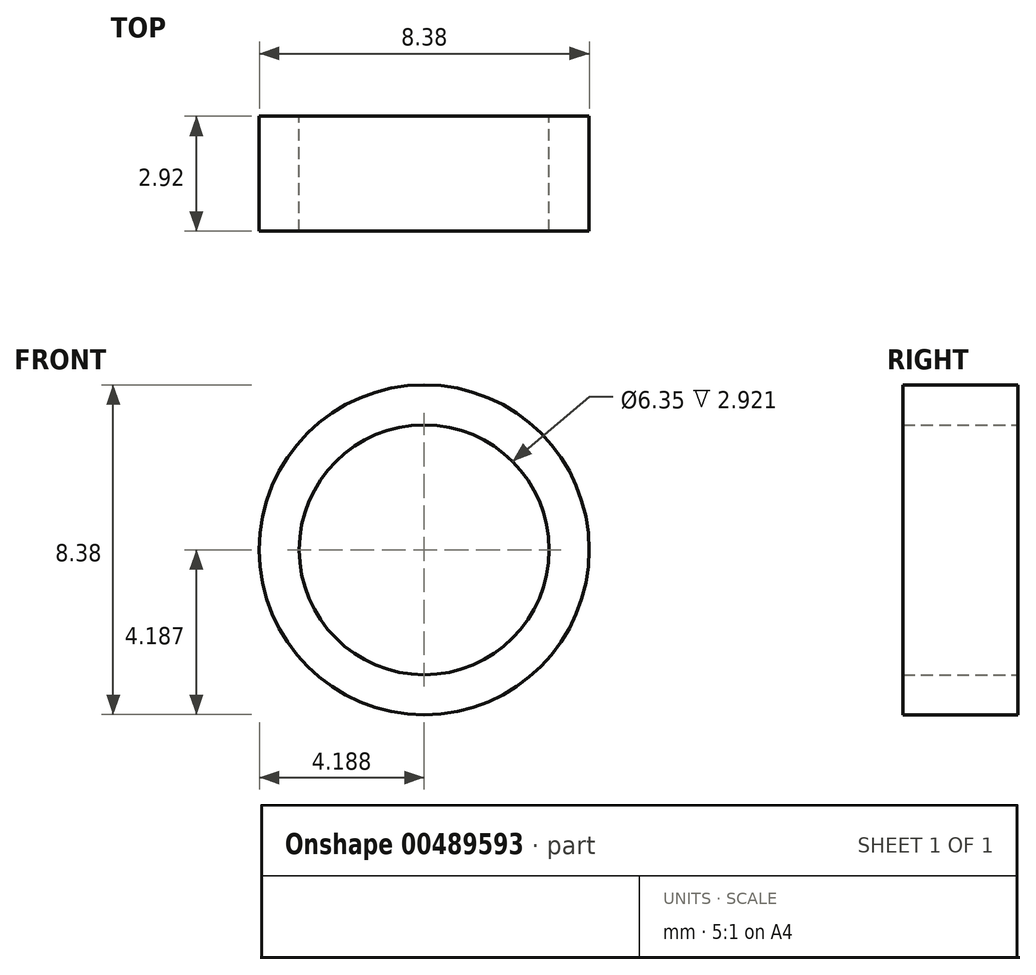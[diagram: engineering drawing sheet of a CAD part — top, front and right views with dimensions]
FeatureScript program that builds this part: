
annotation { "Feature Type Name" : "Feature", "Feature Type Description" : "" }
export const myFeature = defineFeature(function(context is Context, id is Id, definition is map)
    precondition{}
    {
        {
            var Q0;
            Q0=qCreatedBy(makeId("Front.planeOp"),FACE);
            var sketch = newSketch(context, id + "F0", { "sketchPlane" : qUnion([Q0])});
            skCircle(sketch, "E0", {"center": v(-18.63, 27.13) * mm, "radius": 4.2 * mm});
            skCircle(sketch, "E1", {"center": v(-18.63, 27.13) * mm, "radius": 3.18 * mm});
            skSolve(sketch);
        }
        {
            var Q0;
            Q0=makeQuery(id+"F0.imprint","IMPRINT",FACE,{"disambiguationData":[TD([[makeQuery(id+"F0.imprint","IMPRINT",EDGE,{"derivedFrom":sQuery(id+"F0.wireOp",EDGE,"E0")}),1.0]])]});
            extrude(context, id + "F1", {"entities" : qUnion([Q0]), "depth" : 2.92 * mm, "offsetDistance" : 25.4 * mm});
        }
    });
